# Revit family: Grohe_ShowerMixer_Essence_25252KF1
name_source: partatom
category: Plumbing Fixtures
units: mm (PartAtom-declared; Revit-internal decimal feet)

## family parameters
Cut with Voids When Loaded = No
Host = Face
OmniClass Number = 23.45.05.00
OmniClass Title = Sanitary Equipment
Part Type = Normal
Room Calculation Point = No
Round Connector Dimension = Use Diameter
Shared = No

## types (1)
- ESSENCE Shower Mixer (25252KF1)
    Assembly Code = D2010
    AssetType = Fixed
    BIMObjectName = Grohe_ShowerMixer_Essence_25252KF1
    CO2NeutralProduction = GROHE is one of the first leading manufacturer within the sanitary industry having a CO2-neutral production.
    CW Connection = Yes
    ClassificationName = Uniclass2015
    ClassificationValue = Pr_40_20_87_78
    Color = Matt Black
    Cost = 0 $
    Default Elevation = 0 mm  [stored 0 ft]
    Description = ESSENCE Shower Mixer
    DimensionsDocumentLink = https://cdn.cloud.grohe.com
    DocumentationCertificates = https://www.bimstore.co
    DocumentationInstallationGuide = https://www.bimstore.co
    DocumentationLiterature = https://www.bimstore.co
    DocumentationMaintenance = https://www.bimstore.co
    DocumentationTechnical = https://www.bimstore.co
    DurationUnit = Years
    EF000003 = Wall
    EF000139 = Other
    EF001707 = 70 °C
    EF002149 = FALSE
    EF002286 = External thread
    EF002671 = Black
    EF007955 = TRUE
    EF011775 = EB
    EF011779 = FALSE
    EF012753 = 27.0
    EF014578 = FALSE
    EF014591 = FALSE
    EF016731 = Group I,<= 20 dB(A)
    EF020105 = No
    EF020259 = Downwards
    EF020780 = Single-grip
    EF020781 = Cartouche, ceramic
    EF020785 = 1/2 inch
    EF020787 = Group II, <=30 dB(A)
    EF020788 = FALSE
    EF020791 = Brass
    EF020799 = TRUE
    EF020805 = FALSE
    EF020967 = FALSE
    EF021035 = FALSE
    EF021835 = 150 mm
    EF021855 = FALSE
    EF022042 = C
    EF022337 = 1/2 inch
    EF023686 = not applicable
    EF023687 = FALSE
    EF023688 = not relevant
    EF023957 = FALSE
    EF024919 = FALSE
    EF025109 = Other
    EFDE0022 = Group I, <=20 dB(A)
    EFNL0001 = FALSE
    EFSE0002 = FALSE
    Ecojoy = No
    ExpectedLife = 0
    FullRecyclabilityOfPlastic = All plastic components are fully recyclable
    GROHESocialCommittment = green.grohe.com/social_engagement
    GROHESustainability = green.grohe.com
    HW Connection = Yes
    IfcExportAs = IfcPipeFitting
    IfcExportType = IfcPipeFittingType
    Keynote = N13
    Manufacturer = Grohe
    ManufacturerName = Grohe
    Model = ESSENCE Shower Mixer
    ModelNumber = 25252KF1
    ModelReference = ESSENCE Shower Mixer
    NBSDescription = Shower mixers
    NBSObjectName = Grohe - Shower mixers
    NBSReference = 45-35-70/335
    NominalDepth = 0 mm  [stored 0 ft]
    NominalHeight = 0 mm  [stored 0 ft]
    NominalLength = 0 mm  [stored 0 ft]
    PQDiagramLink = https://cdn.cloud.grohe.com
    PrimaryMaterial = Grohe_MattBlack
    ProductDescription = wall mounted

metal lever

GROHE SilkMove 35 mm ceramic cartridge

with temperature limiter

GROHE Long-Life Shine finish

shower outlet 1/2"

integrated non-return valve

S-unions

protected against backflow

min. recommended pressure 1.0 bar

professional exclusive
    ProductNumber = 25252KF1
    ProductPageURL = https://www.grohe.co.uk
    ProductShortText = Essence Single-lever shower mixer 1/2"
    ProductType = Single Lever Mixer
    ProductionYear = 2023
    SustainabilityAward = green.grohe.com/awards
    SustainabilityReport = green.grohe.com/reporting
    TPIDocumentLink = https://cdn.cloud.grohe.com
    Type Comments = ESSENCE Shower Mixer
    TypeName = ESSENCE Shower Mixer
    URL = https://www.grohe.co.uk
    Vent Connection = No
    WarrantyDurationLabor = 0
    WarrantyDurationParts = 0
    WarrantyDurationUnit = Years
    Waste Connection = No
    _BSBibleVersion = 17
    _BimSpecGuid = 0
    _CurrentRevision = 1
    _DistributedBy = https://www.bimstore.co
    _ObjectUserGuide = https://www.bimstore.co

note: [stored X ft] marks values corroborated as IEEE doubles in the binary element streams (Revit-internal decimal feet)

## geometry (parser evidence)
native form markers: Sweep x2
no freeform markers — native parametric forms only
